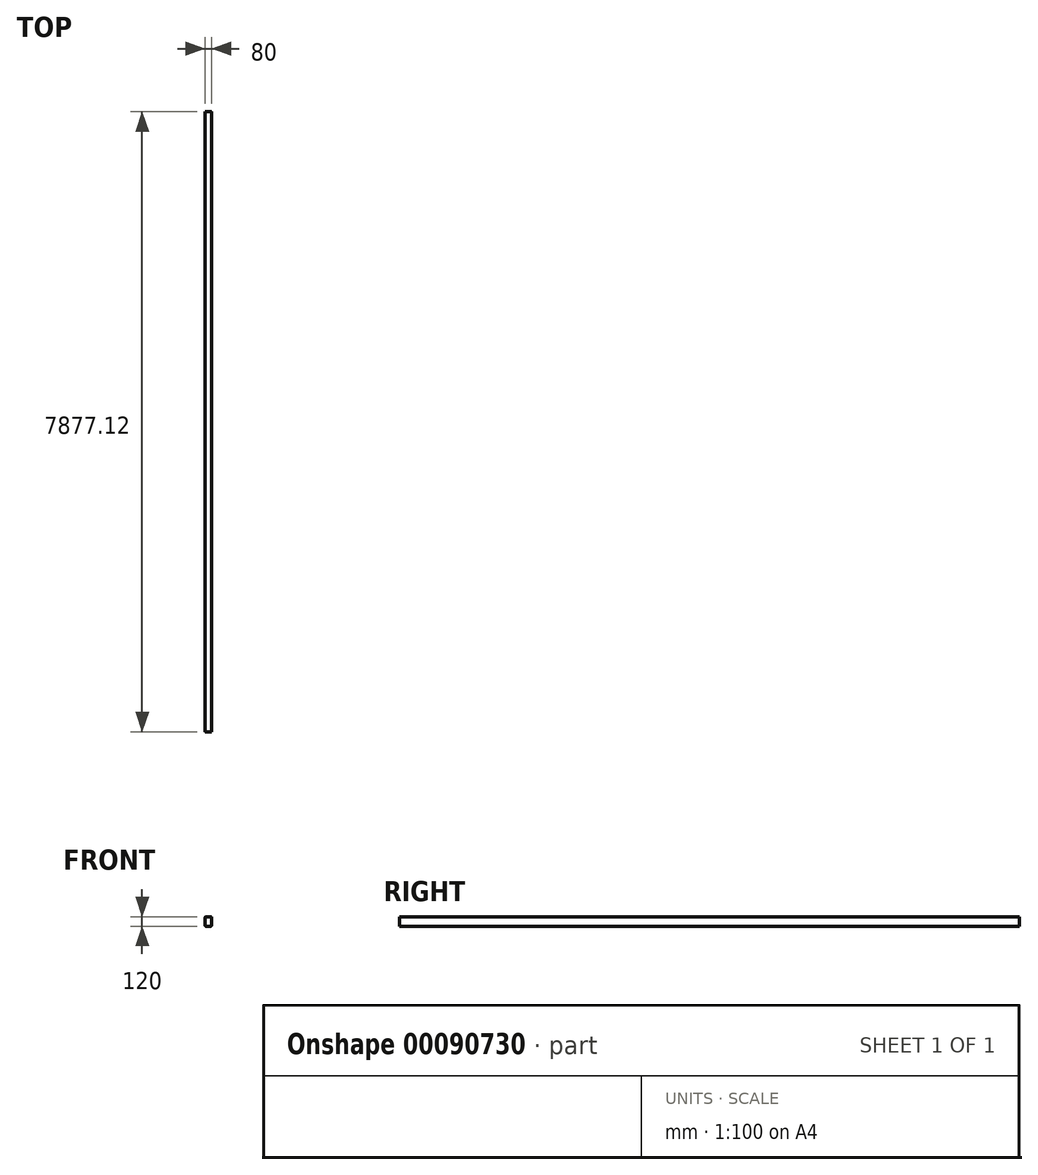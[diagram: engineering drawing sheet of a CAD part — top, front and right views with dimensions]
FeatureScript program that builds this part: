
annotation { "Feature Type Name" : "Feature", "Feature Type Description" : "" }
export const myFeature = defineFeature(function(context is Context, id is Id, definition is map)
    precondition{}
    {
        {
            var Q0;
            Q0=qCreatedBy(makeId("Front.planeOp"),FACE);
            var sketch = newSketch(context, id + "F0", { "sketchPlane" : qUnion([Q0])});
            skLineSegment(sketch, "E0.bottom", {"start": v(-29.78, 60.33) * mm, "end": v(30.22, 60.33) * mm});
            skLineSegment(sketch, "E0.top", {"start": v(-29.78, -59.67) * mm, "end": v(30.22, -59.67) * mm});
            skLineSegment(sketch, "E0.left", {"start": v(-39.78, 50.33) * mm, "end": v(-39.78, -49.67) * mm});
            skLineSegment(sketch, "E0.right", {"start": v(40.22, 50.33) * mm, "end": v(40.22, -49.67) * mm});
            skPoint(sketch, "E0.middle", {"position": v(0.22, 0.33) * mm});
            skPoint(sketch, "E1.visualSharp", {"position": v(-39.78, 60.33) * mm});
            skArc(sketch, "E1.filletArc", {"start": v(-29.78, 60.33) * mm, "mid": v(-36.85, 57.4) * mm, "end": v(-39.78, 50.33) * mm});
            skPoint(sketch, "E2.visualSharp", {"position": v(40.22, 60.33) * mm});
            skArc(sketch, "E2.filletArc", {"start": v(40.22, 50.33) * mm, "mid": v(37.3, 57.4) * mm, "end": v(30.22, 60.33) * mm});
            skPoint(sketch, "E3.visualSharp", {"position": v(40.22, -59.67) * mm});
            skArc(sketch, "E3.filletArc", {"start": v(30.22, -59.67) * mm, "mid": v(37.3, -56.74) * mm, "end": v(40.22, -49.67) * mm});
            skPoint(sketch, "E4.visualSharp", {"position": v(-39.78, -59.67) * mm});
            skArc(sketch, "E4.filletArc", {"start": v(-39.78, -49.67) * mm, "mid": v(-36.85, -56.74) * mm, "end": v(-29.78, -59.67) * mm});
            skLineSegment(sketch, "E5.0", {"start": v(-29.78, 55.33) * mm, "end": v(30.22, 55.33) * mm});
            skLineSegment(sketch, "E6.0", {"start": v(35.22, 50.33) * mm, "end": v(35.22, -49.67) * mm});
            skLineSegment(sketch, "E7.0", {"start": v(-29.78, -54.67) * mm, "end": v(30.22, -54.67) * mm});
            skArc(sketch, "E8.0", {"start": v(-34.78, -49.67) * mm, "mid": v(-33.31, -53.2) * mm, "end": v(-29.78, -54.67) * mm});
            skLineSegment(sketch, "E8.1", {"start": v(-34.78, 50.33) * mm, "end": v(-34.78, -49.67) * mm});
            skArc(sketch, "E8.2", {"start": v(-29.78, 55.33) * mm, "mid": v(-33.31, 53.87) * mm, "end": v(-34.78, 50.33) * mm});
            skArc(sketch, "E8.3", {"start": v(30.22, -54.67) * mm, "mid": v(33.76, -53.2) * mm, "end": v(35.22, -49.67) * mm});
            skArc(sketch, "E8.5", {"start": v(35.22, 50.33) * mm, "mid": v(33.76, 53.87) * mm, "end": v(30.22, 55.33) * mm});
            skText(sketch, "E9", { "text": "TRAILER\n\n", "fontName": "OpenSans-Regular.ttf"});
            const initialGuessF0  = {"E9": [-0.0863, 0.02766, 1, 0, 0.00714]};
            skSetInitialGuess(sketch, initialGuessF0);
            skSolve(sketch);
        }
        {
            var Q0;
            Q0=makeQuery(id+"F0.imprint","IMPRINT",FACE,{"disambiguationData":[TD([[makeQuery(id+"F0.imprint","IMPRINT",EDGE,{"derivedFrom":sQuery(id+"F0.wireOp",EDGE,"E7.0")}),1.0]])]});
            var Q1;
            Q1=makeQuery(id+"F0.imprint","IMPRINT",FACE,{"disambiguationData":[TD([[makeQuery(id+"F0.imprint","IMPRINT",EDGE,{"derivedFrom":sQuery(id+"F0.wireOp",EDGE,"E0.bottom")}),-1.0]])]});
            extrude(context, id + "F1", {"entities" : qUnion([Q0, Q1]), "depth" : 7877.12 * mm});
        }
    });
